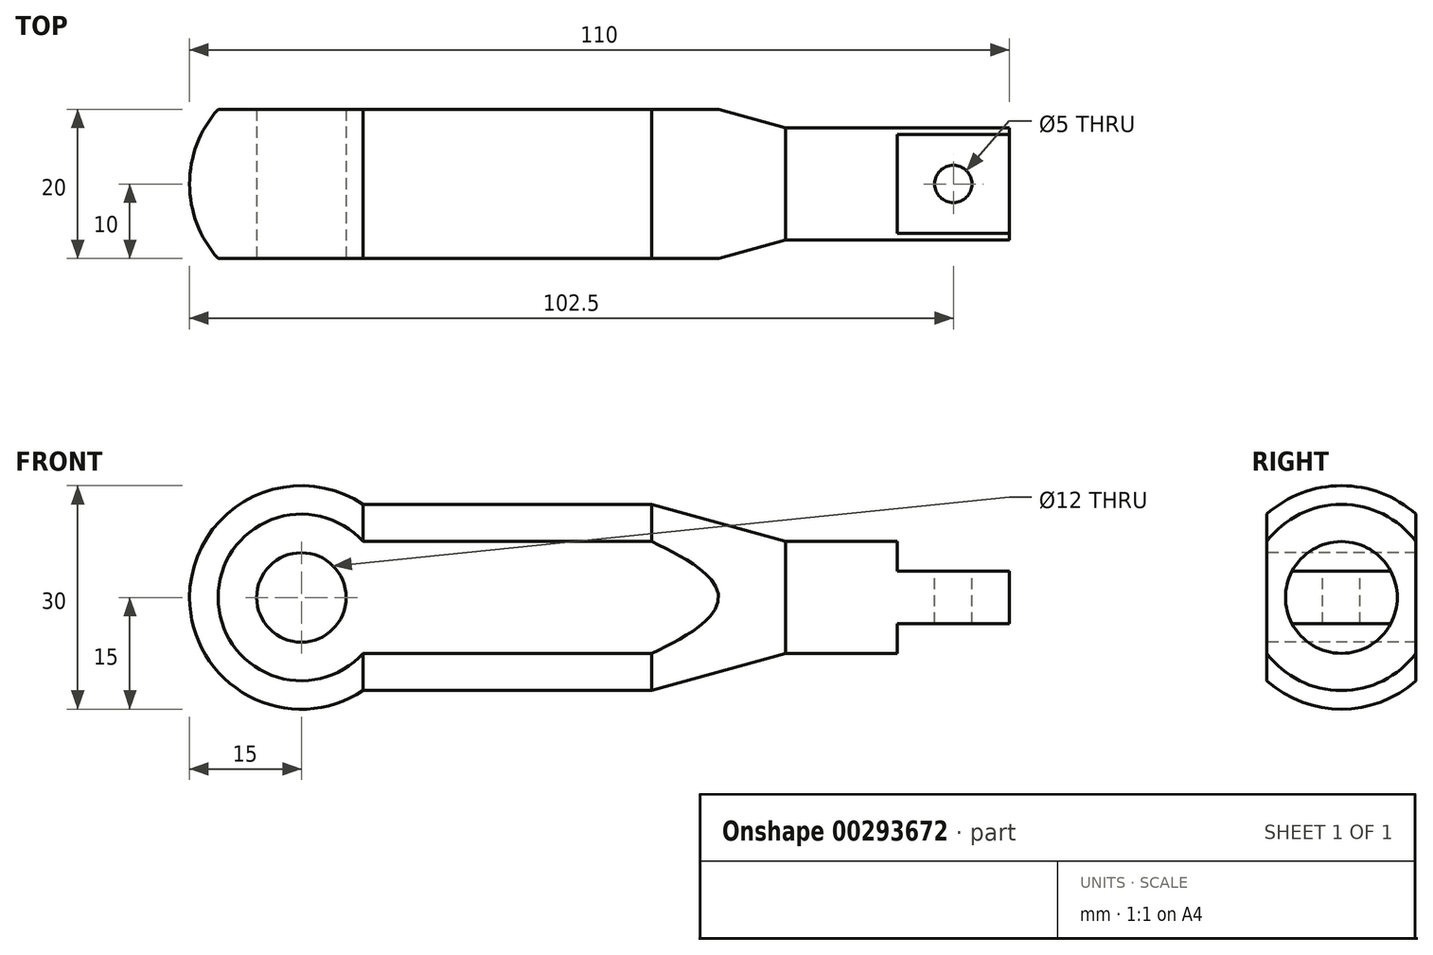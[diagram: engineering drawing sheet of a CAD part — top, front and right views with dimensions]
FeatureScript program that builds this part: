
annotation { "Feature Type Name" : "Feature", "Feature Type Description" : "" }
export const myFeature = defineFeature(function(context is Context, id is Id, definition is map)
    precondition{}
    {
        {
            var Q0;
            Q0=qCreatedBy(makeId("Front.planeOp"),FACE);
            var sketch = newSketch(context, id + "F0", { "sketchPlane" : qUnion([Q0])});
            skCircle(sketch, "E0", {"center": v(0, 0) * mm, "radius": 15 * mm});
            skLineSegment(sketch, "E1", {"start": v(8.3, 12.5) * mm, "end": v(47, 12.5) * mm});
            skLineSegment(sketch, "E2", {"start": v(47, 12.5) * mm, "end": v(65, 7.5) * mm});
            skLineSegment(sketch, "E3.MirrorCS", {"start": v(8.3, -12.5) * mm, "end": v(47, -12.5) * mm});
            skLineSegment(sketch, "E4.MirrorCS", {"start": v(47, -12.5) * mm, "end": v(65, -7.5) * mm});
            skLineSegment(sketch, "E5", {"start": v(-15, 0) * mm, "end": v(95, 0) * mm, "construction": true});
            skLineSegment(sketch, "E6", {"start": v(95, 0) * mm, "end": v(-15, 0) * mm});
            skCircle(sketch, "E7", {"center": v(0, 0) * mm, "radius": 6 * mm});
            skLineSegment(sketch, "E8", {"start": v(65, 7.5) * mm, "end": v(95, 7.5) * mm});
            skLineSegment(sketch, "E9", {"start": v(95, 7.5) * mm, "end": v(95, 0) * mm});
            skLineSegment(sketch, "E10.MirrorCS", {"start": v(65, -7.5) * mm, "end": v(95, -7.5) * mm});
            skLineSegment(sketch, "E11.MirrorCS", {"start": v(95, -7.5) * mm, "end": v(95, 0) * mm});
            skSolve(sketch);
        }
        {
            var Q0;
            {var subQ0=sQuery(id+"F0.wireOp",EDGE,"E1");Q0=makeQuery(id+"F0.imprint","IMPRINT",FACE,{"disambiguationData":[TD([[makeQuery(id+"F0.imprint","IMPRINT",EDGE,{"derivedFrom":subQ0}),-1.0]])]});}
            var Q1;
            {var subQ0=sQuery(id+"F0.wireOp",EDGE,"E0");var subQ1=makeQuery(id+"F0.imprint","INTERSECT",VERTEX,{"derivedFrom":[subQ0,sQuery(id+"F0.wireOp",EDGE,"E1")]});Q1=makeQuery(id+"F0.imprint","IMPRINT",FACE,{"disambiguationData":[TD([[makeQuery(id+"F0.imprint","IMPRINT",EDGE,{"disambiguationData":[TD([[subQ1,1.0]])],"derivedFrom":subQ0}),1.0]])]});}
            var Q2;
            Q2=sQuery(id+"F0.wireOp",EDGE,"E6");
            revolve(context, id + "F1", {"entities" : qUnion([Q0, Q1]), "axis" : qUnion([Q2]), "revolveType" : RevolveType.FULL});
        }
        {
            var Q0;
            {var subQ0=sQuery(id+"F0.wireOp",EDGE,"E7");var subQ1=sQuery(id+"F0.wireOp",EDGE,"E6");var subQ2=makeQuery(id+"F0.imprint","INTERSECT",VERTEX,{"disambiguationData":[OD(0.0)],"derivedFrom":[subQ1,subQ0]});Q0=makeQuery(id+"F0.imprint","IMPRINT",FACE,{"disambiguationData":[TD([[makeQuery(id+"F0.imprint","IMPRINT",EDGE,{"disambiguationData":[TD([[subQ2,-1.0]])],"derivedFrom":subQ1}),1.0]])]});}
            var Q1;
            {var subQ0=sQuery(id+"F0.wireOp",EDGE,"E7");var subQ1=sQuery(id+"F0.wireOp",EDGE,"E6");var subQ2=makeQuery(id+"F0.imprint","INTERSECT",VERTEX,{"disambiguationData":[OD(0.0)],"derivedFrom":[subQ1,subQ0]});Q1=makeQuery(id+"F0.imprint","IMPRINT",FACE,{"disambiguationData":[TD([[makeQuery(id+"F0.imprint","IMPRINT",EDGE,{"disambiguationData":[TD([[subQ2,-1.0]])],"derivedFrom":subQ1}),-1.0]])]});}
            var Q2;
            Q2=makeQuery(id+"F1.opRevolve","SWEPT_FACE",FACE,{"disambiguationData":[OSD([sQuery(id+"F0.wireOp",EDGE,"E0")])]});
            extrude(context, id + "F2", {"entities" : qUnion([Q0, Q1]), "operationType" : NewBodyOperationType.REMOVE, "endBound" : BoundingType.THROUGH_ALL, "oppositeDirection" : true, "depth" : 25 * mm, "hasSecondDirection" : true, "secondDirectionBound" : SecondDirectionBoundingType.UP_TO_SURFACE, "secondDirectionOppositeDirection" : false, "secondDirectionBoundEntityFace" : qUnion([Q2]), "secondDirectionDepth" : 25 * mm});
        }
        {
            var Q0;
            Q0=makeQuery(id+"F1.opRevolve","SWEPT_FACE",FACE,{"disambiguationData":[OSD([sQuery(id+"F0.wireOp",EDGE,"E9")])]});
            var sketch = newSketch(context, id + "F3", { "sketchPlane" : qUnion([Q0])});
            skLineSegment(sketch, "E12", {"start": v(-6.63, 3.5) * mm, "end": v(6.63, 3.5) * mm});
            skLineSegment(sketch, "E13", {"start": v(-7.5, 0) * mm, "end": v(7.5, 0) * mm, "construction": true});
            skLineSegment(sketch, "E14.MirrorCS", {"start": v(-6.63, -3.5) * mm, "end": v(6.63, -3.5) * mm});
            skLineSegment(sketch, "E15", {"start": v(10, 11.62) * mm, "end": v(10, -11.38) * mm});
            skLineSegment(sketch, "E16", {"start": v(0, 0) * mm, "end": v(0, 19.03) * mm, "construction": true});
            skPoint(sketch, "E16.endSnap0", {"position": v(0, 0) * mm});
            skLineSegment(sketch, "E17", {"start": v(0, 19.03) * mm, "end": v(0, -14.38) * mm, "construction": true});
            skPoint(sketch, "E17.endSnap0", {"position": v(0, -3.5) * mm});
            skLineSegment(sketch, "E18.MirrorCS", {"start": v(-10, 11.62) * mm, "end": v(-10, -11.38) * mm});
            skSolve(sketch);
        }
        {
            var Q0;
            {var subQ0=sQuery(id+"F3.wireOp",EDGE,"E12");Q0=makeQuery(id+"F3.imprint","IMPRINT",FACE,{"disambiguationData":[TD([[makeQuery(id+"F3.imprint","IMPRINT",EDGE,{"derivedFrom":subQ0}),1.0]])]});}
            var Q1;
            {var subQ0=sQuery(id+"F3.wireOp",EDGE,"E14.MirrorCS");Q1=makeQuery(id+"F3.imprint","IMPRINT",FACE,{"disambiguationData":[TD([[makeQuery(id+"F3.imprint","IMPRINT",EDGE,{"derivedFrom":subQ0}),-1.0]])]});}
            extrude(context, id + "F4", {"entities" : qUnion([Q0, Q1]), "operationType" : NewBodyOperationType.REMOVE, "oppositeDirection" : true, "depth" : 15 * mm});
        }
        {
            var Q0;
            Q0=makeQuery(id+"F4.boolean.opBoolean","COPY",FACE,{"derivedFrom":makeQuery(id+"F4.opExtrude","SWEPT_FACE",FACE,{"disambiguationData":[OSD([sQuery(id+"F3.wireOp",EDGE,"E12")])]})});
            var sketch = newSketch(context, id + "F5", { "sketchPlane" : qUnion([Q0])});
            skCircle(sketch, "E19", {"center": v(87.5, 0) * mm, "radius": 2.5 * mm});
            skSolve(sketch);
        }
        {
            var Q0;
            Q0=makeQuery(id+"F5.imprint","IMPRINT",FACE,{"disambiguationData":[TD([[makeQuery(id+"F5.imprint","IMPRINT",EDGE,{"derivedFrom":sQuery(id+"F5.wireOp",EDGE,"E19")}),1.0]])]});
            var Q1;
            Q1=makeQuery(id+"F4.boolean.opBoolean","COPY",FACE,{"derivedFrom":makeQuery(id+"F4.opExtrude","SWEPT_FACE",FACE,{"disambiguationData":[OSD([sQuery(id+"F3.wireOp",EDGE,"E14.MirrorCS")])]})});
            extrude(context, id + "F6", {"entities" : qUnion([Q0]), "operationType" : NewBodyOperationType.REMOVE, "endBound" : BoundingType.UP_TO_SURFACE, "oppositeDirection" : true, "endBoundEntityFace" : qUnion([Q1]), "depth" : 25 * mm});
        }
        {
            var Q0;
            Q0=qCreatedBy(makeId("Right.planeOp"),FACE);
            var sketch = newSketch(context, id + "F7", { "sketchPlane" : qUnion([Q0])});
            skLineSegment(sketch, "E20", {"start": v(10, 12) * mm, "end": v(10, -12) * mm});
            skLineSegment(sketch, "E21", {"start": v(-10, 12) * mm, "end": v(-10, -12) * mm});
            skLineSegment(sketch, "E22", {"start": v(-10, 12) * mm, "end": v(-20, 12) * mm});
            skLineSegment(sketch, "E23", {"start": v(-20, 12) * mm, "end": v(-20, -12) * mm});
            skLineSegment(sketch, "E24", {"start": v(-20, -12) * mm, "end": v(-10, -12) * mm});
            skLineSegment(sketch, "E25", {"start": v(10, 12) * mm, "end": v(20, 12) * mm});
            skLineSegment(sketch, "E26", {"start": v(20, 12) * mm, "end": v(20, -12) * mm});
            skLineSegment(sketch, "E27", {"start": v(20, -12) * mm, "end": v(10, -12) * mm});
            skSolve(sketch);
        }
        {
            var Q0;
            Q0=makeQuery(id+"F7.imprint","IMPRINT",FACE,{"disambiguationData":[TD([[makeQuery(id+"F7.imprint","IMPRINT",EDGE,{"derivedFrom":sQuery(id+"F7.wireOp",EDGE,"E21")}),-1.0]])]});
            var Q1;
            Q1=makeQuery(id+"F7.imprint","IMPRINT",FACE,{"disambiguationData":[TD([[makeQuery(id+"F7.imprint","IMPRINT",EDGE,{"derivedFrom":sQuery(id+"F7.wireOp",EDGE,"E20")}),1.0]])]});
            extrude(context, id + "F8", {"entities" : qUnion([Q0, Q1]), "operationType" : NewBodyOperationType.REMOVE, "endBound" : BoundingType.THROUGH_ALL, "oppositeDirection" : true, "depth" : 25 * mm, "hasSecondDirection" : true, "secondDirectionBound" : SecondDirectionBoundingType.THROUGH_ALL, "secondDirectionOppositeDirection" : false, "secondDirectionDepth" : 25 * mm});
        }
    });
